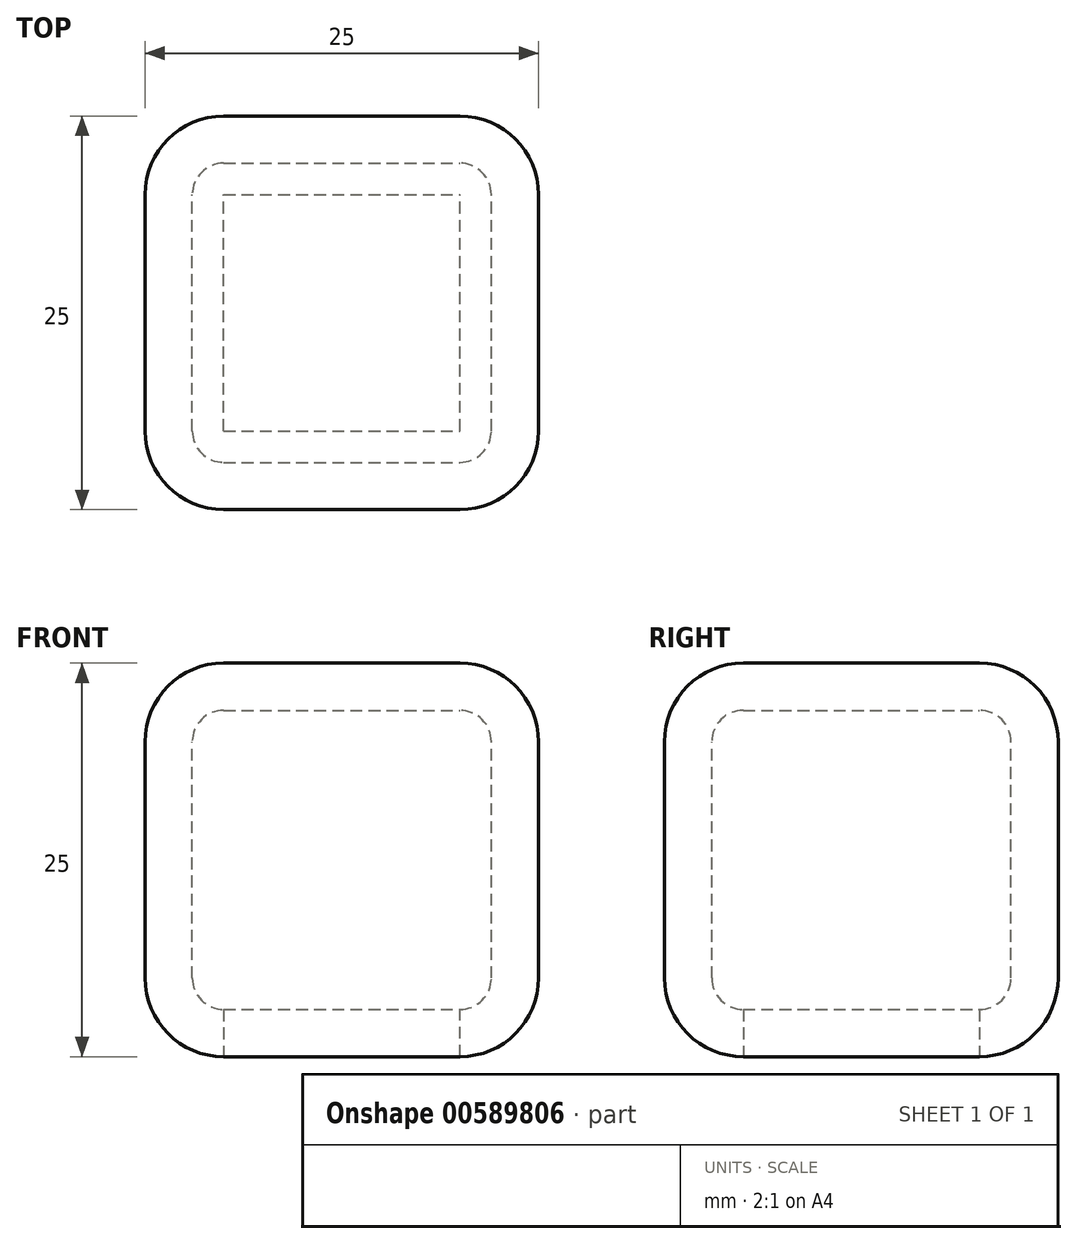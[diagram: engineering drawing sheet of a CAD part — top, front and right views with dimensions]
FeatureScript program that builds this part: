
annotation { "Feature Type Name" : "Feature", "Feature Type Description" : "" }
export const myFeature = defineFeature(function(context is Context, id is Id, definition is map)
    precondition{}
    {
        {
            var Q0;
            Q0=qCreatedBy(makeId("Top.planeOp"),FACE);
            var sketch = newSketch(context, id + "F0", { "sketchPlane" : qUnion([Q0])});
            skLineSegment(sketch, "E0.bottom", {"start": v(0, 0) * mm, "end": v(25, 0) * mm});
            skLineSegment(sketch, "E0.top", {"start": v(0, 25) * mm, "end": v(25, 25) * mm});
            skLineSegment(sketch, "E0.left", {"start": v(0, 0) * mm, "end": v(0, 25) * mm});
            skLineSegment(sketch, "E0.right", {"start": v(25, 0) * mm, "end": v(25, 25) * mm});
            skSolve(sketch);
        }
        {
            var Q0;
            Q0 = qSketchRegion(id + "F0", true);
            extrude(context, id + "F1", {"entities" : qUnion([Q0]), "depth" : 25 * mm, "offsetDistance" : 25 * mm});
        }
        {
            var Q0;
            Q0=makeQuery(id+"F1.opExtrude","CAP_EDGE",EDGE,{"disambiguationData":[OSD([sQuery(id+"F0.wireOp",EDGE,"E0.bottom")])],"isStart":true});
            var Q1;
            Q1=makeQuery(id+"F1.opExtrude","SWEPT_EDGE",EDGE,{"disambiguationData":[OSD([sQuery(id+"F0.wireOp",EDGE,"E0.bottom"),sQuery(id+"F0.wireOp",EDGE,"E0.right")])]});
            var Q2;
            Q2=makeQuery(id+"F1.opExtrude","CAP_EDGE",EDGE,{"disambiguationData":[OSD([sQuery(id+"F0.wireOp",EDGE,"E0.bottom")])],"isStart":false});
            var Q3;
            Q3=makeQuery(id+"F1.opExtrude","SWEPT_EDGE",EDGE,{"disambiguationData":[OSD([sQuery(id+"F0.wireOp",EDGE,"E0.top"),sQuery(id+"F0.wireOp",EDGE,"E0.right")])]});
            var Q4;
            Q4=makeQuery(id+"F1.opExtrude","CAP_EDGE",EDGE,{"disambiguationData":[OSD([sQuery(id+"F0.wireOp",EDGE,"E0.right")])],"isStart":true});
            var Q5;
            Q5=makeQuery(id+"F1.opExtrude","CAP_EDGE",EDGE,{"disambiguationData":[OSD([sQuery(id+"F0.wireOp",EDGE,"E0.right")])],"isStart":false});
            var Q6;
            Q6=makeQuery(id+"F1.opExtrude","SWEPT_FACE",FACE,{"disambiguationData":[OSD([sQuery(id+"F0.wireOp",EDGE,"E0.left")])]});
            var Q7;
            Q7=makeQuery(id+"F1.opExtrude","SWEPT_FACE",FACE,{"disambiguationData":[OSD([sQuery(id+"F0.wireOp",EDGE,"E0.top")])]});
            fillet(context, id + "F2", {"entities" : qUnion([Q0, Q1, Q2, Q3, Q4, Q5, Q6, Q7]), "radius" : 5 * mm, "tangentPropagation" : true, "allowEdgeOverflow" : false});
        }
        {
            var Q0;
            Q0=makeQuery(id+"F1.opExtrude","CAP_FACE",FACE,{"disambiguationData":[OSD([sQuery(id+"F0.wireOp",EDGE,"E0.bottom"),sQuery(id+"F0.wireOp",EDGE,"E0.top"),sQuery(id+"F0.wireOp",EDGE,"E0.left"),sQuery(id+"F0.wireOp",EDGE,"E0.right")])],"isStart":true});
            shell(context, id + "F3", {"entities" : qUnion([Q0]), "thickness" : 3 * mm});
        }
    });
